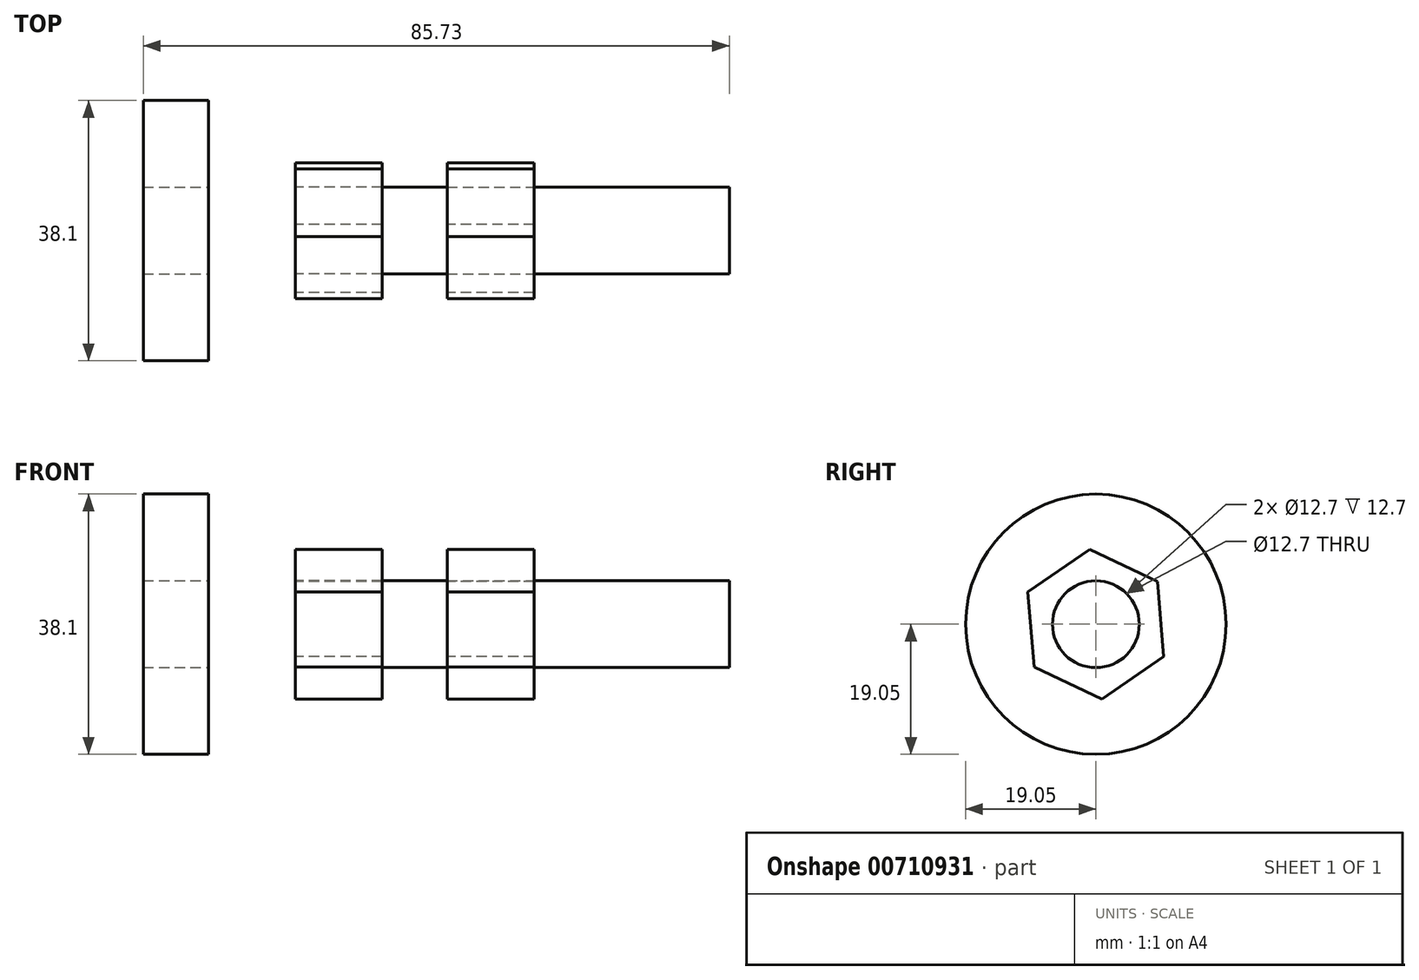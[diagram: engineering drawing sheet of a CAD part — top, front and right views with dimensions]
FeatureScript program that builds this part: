
annotation { "Feature Type Name" : "Feature", "Feature Type Description" : "" }
export const myFeature = defineFeature(function(context is Context, id is Id, definition is map)
    precondition{}
    {
        {
            var Q0;
            Q0=qCreatedBy(makeId("Right.planeOp"),FACE);
            var sketch = newSketch(context, id + "F0", { "sketchPlane" : qUnion([Q0])});
            skCircle(sketch, "E0", {"center": v(0, 0) * mm, "radius": 19.05 * mm});
            skSolve(sketch);
        }
        {
            var Q0;
            Q0 = qSketchRegion(id + "F0", true);
            extrude(context, id + "F1", {"entities" : qUnion([Q0]), "oppositeDirection" : true, "depth" : 9.52 * mm, "offsetDistance" : 25.4 * mm});
        }
        {
            var Q0;
            Q0=makeQuery(id+"F1.opExtrude","CAP_FACE",FACE,{"disambiguationData":[OSD([sQuery(id+"F0.wireOp",EDGE,"E0")])],"isStart":true});
            var sketch = newSketch(context, id + "F2", { "sketchPlane" : qUnion([Q0])});
            skCircle(sketch, "E1", {"center": v(0, 0) * mm, "radius": 6.35 * mm});
            skSolve(sketch);
        }
        {
            var Q0;
            Q0 = qSketchRegion(id + "F2", true);
            extrude(context, id + "F3", {"entities" : qUnion([Q0]), "operationType" : NewBodyOperationType.ADD, "depth" : 76.2 * mm, "offsetDistance" : 25.4 * mm});
        }
        {
            var Q0;
            Q0=qCreatedBy(makeId("Right.planeOp"),FACE);
            var sketch = newSketch(context, id + "F4", { "sketchPlane" : qUnion([Q0])});
            skCircle(sketch, "E2.cCircle", {"center": v(0, 0) * mm, "radius": 9.53 * mm, "construction": true});
            skLineSegment(sketch, "E2.0", {"start": v(-9.94, 4.7) * mm, "end": v(-0.9, 10.96) * mm});
            skLineSegment(sketch, "E2.1", {"start": v(-0.9, 10.96) * mm, "end": v(9.05, 6.26) * mm});
            skLineSegment(sketch, "E2.2", {"start": v(9.05, 6.26) * mm, "end": v(9.94, -4.7) * mm});
            skLineSegment(sketch, "E2.3", {"start": v(9.94, -4.7) * mm, "end": v(0.9, -10.96) * mm});
            skLineSegment(sketch, "E2.4", {"start": v(0.9, -10.96) * mm, "end": v(-9.05, -6.26) * mm});
            skLineSegment(sketch, "E2.5", {"start": v(-9.05, -6.26) * mm, "end": v(-9.94, 4.7) * mm});
            skPoint(sketch, "E2.0.midPoint", {"position": v(-5.42, 7.83) * mm});
            skSolve(sketch);
        }
        {
            var Q0;
            Q0 = qSketchRegion(id + "F4", true);
            extrude(context, id + "F5", {"entities" : qUnion([Q0]), "depth" : 12.7 * mm, "offsetDistance" : 25.4 * mm});
        }
        {
            var Q0;
            Q0=makeQuery(id+"F5.opExtrude","CAP_FACE",FACE,{"disambiguationData":[OSD([sQuery(id+"F4.wireOp",EDGE,"E2.0"),sQuery(id+"F4.wireOp",EDGE,"E2.1"),sQuery(id+"F4.wireOp",EDGE,"E2.2"),sQuery(id+"F4.wireOp",EDGE,"E2.3"),sQuery(id+"F4.wireOp",EDGE,"E2.4"),sQuery(id+"F4.wireOp",EDGE,"E2.5")])],"isStart":false});
            var sketch = newSketch(context, id + "F6", { "sketchPlane" : qUnion([Q0])});
            skCircle(sketch, "E3", {"center": v(0, 0) * mm, "radius": 6.35 * mm});
            skSolve(sketch);
        }
        {
            var Q0;
            Q0 = qSketchRegion(id + "F6", true);
            extrude(context, id + "F7", {"entities" : qUnion([Q0]), "operationType" : NewBodyOperationType.REMOVE, "endBound" : BoundingType.THROUGH_ALL, "oppositeDirection" : true, "depth" : 25.4 * mm, "offsetDistance" : 25.4 * mm});
        }
        {
            var Q0;
            Q0=makeQuery(id+"F5.opExtrude","SWEPT_BODY",BODY,{"disambiguationData":[OSD([sQuery(id+"F4.wireOp",EDGE,"E2.0"),sQuery(id+"F4.wireOp",EDGE,"E2.1"),sQuery(id+"F4.wireOp",EDGE,"E2.2"),sQuery(id+"F4.wireOp",EDGE,"E2.3"),sQuery(id+"F4.wireOp",EDGE,"E2.4"),sQuery(id+"F4.wireOp",EDGE,"E2.5")])]});
            transform(context, id + "F8", {"entities" : qUnion([Q0]), "transformType" : TransformType.TRANSLATION_3D, "dx" : 12.7 * mm, "dy" : 0 * mm, "dz" : 0 * mm, "makeCopy" : false});
        }
        {
            var Q0;
            Q0=makeQuery(id+"F5.opExtrude","SWEPT_BODY",BODY,{"disambiguationData":[OSD([sQuery(id+"F4.wireOp",EDGE,"E2.0"),sQuery(id+"F4.wireOp",EDGE,"E2.1"),sQuery(id+"F4.wireOp",EDGE,"E2.2"),sQuery(id+"F4.wireOp",EDGE,"E2.3"),sQuery(id+"F4.wireOp",EDGE,"E2.4"),sQuery(id+"F4.wireOp",EDGE,"E2.5")])]});
            transform(context, id + "F9", {"entities" : qUnion([Q0]), "transformType" : TransformType.TRANSLATION_3D, "dx" : 22.22 * mm, "dy" : 0 * mm, "dz" : 0 * mm, "makeCopy" : true});
        }
    });
